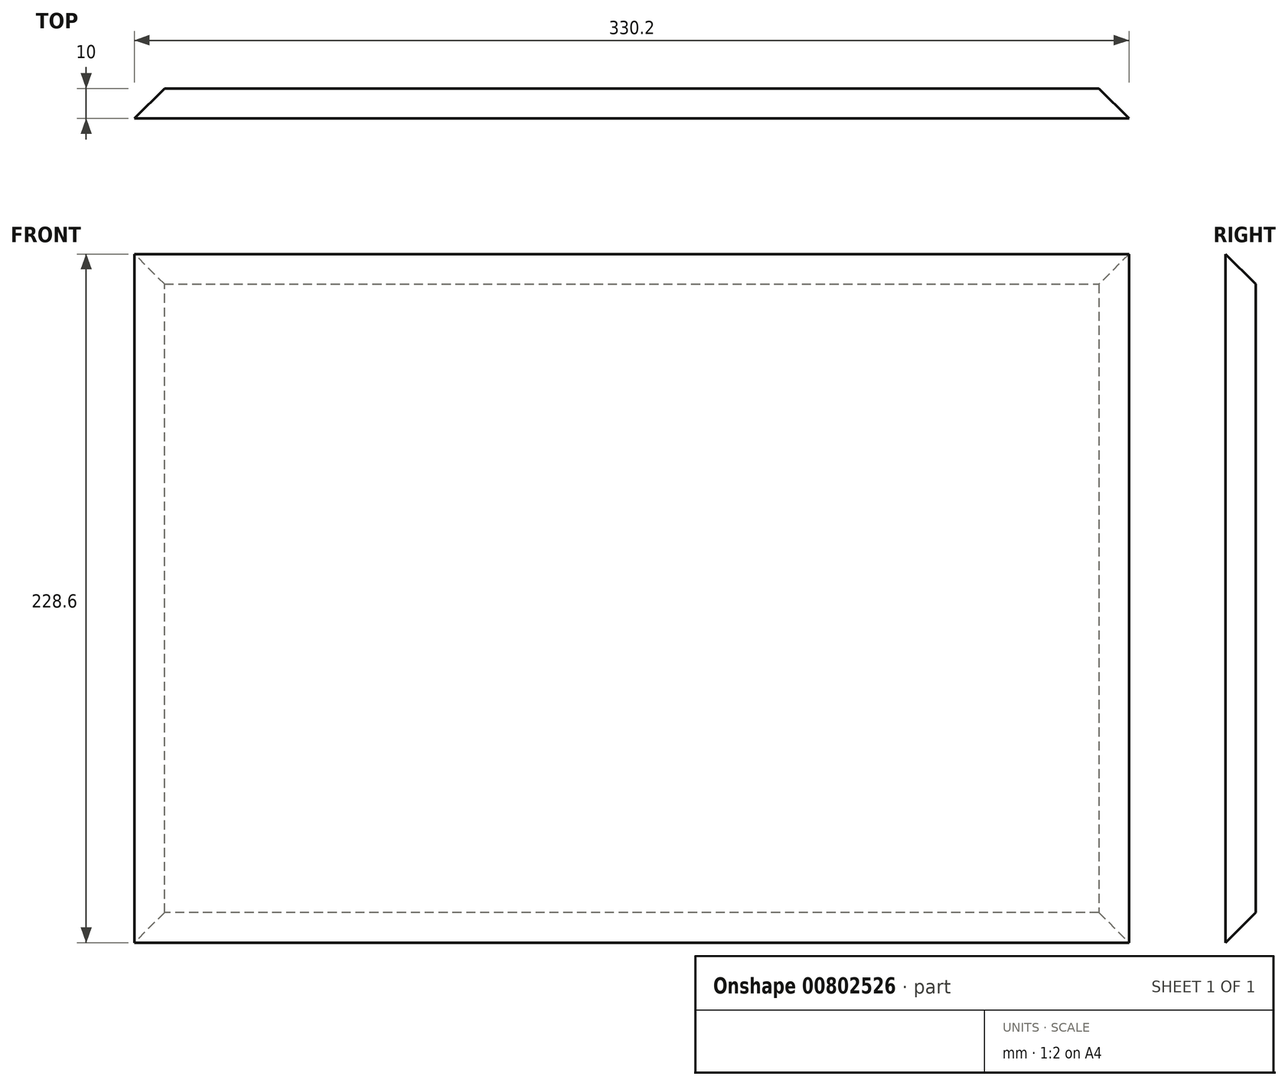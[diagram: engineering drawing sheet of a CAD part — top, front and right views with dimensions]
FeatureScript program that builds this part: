
annotation { "Feature Type Name" : "Feature", "Feature Type Description" : "" }
export const myFeature = defineFeature(function(context is Context, id is Id, definition is map)
    precondition{}
    {
        {
            var Q0;
            Q0=qCreatedBy(makeId("Front.planeOp"),FACE);
            var sketch = newSketch(context, id + "F0", { "sketchPlane" : qUnion([Q0])});
            skLineSegment(sketch, "E0.bottom", {"start": v(165.1, 114.3) * mm, "end": v(-165.1, 114.3) * mm});
            skLineSegment(sketch, "E0.top", {"start": v(165.1, -114.3) * mm, "end": v(-165.1, -114.3) * mm});
            skLineSegment(sketch, "E0.left", {"start": v(165.1, 114.3) * mm, "end": v(165.1, -114.3) * mm});
            skLineSegment(sketch, "E0.right", {"start": v(-165.1, 114.3) * mm, "end": v(-165.1, -114.3) * mm});
            skPoint(sketch, "E0.middle", {"position": v(0, 0) * mm});
            skSolve(sketch);
        }
        {
            var Q0;
            Q0=makeQuery(id+"F0.imprint","IMPRINT",FACE,{"disambiguationData":[TD([[makeQuery(id+"F0.imprint","IMPRINT",EDGE,{"derivedFrom":sQuery(id+"F0.wireOp",EDGE,"E0.bottom")}),1.0]])]});
            var sketch = newSketch(context, id + "F1", { "sketchPlane" : qUnion([Q0])});
            skLineSegment(sketch, "E1", {"start": v(-112.44, 43.6) * mm, "end": v(115.5, 43.6) * mm, "construction": true});
            skLineSegment(sketch, "E2.MirrorCS", {"start": v(-112.44, -43.6) * mm, "end": v(115.5, -43.6) * mm, "construction": true});
            skSolve(sketch);
        }
        {
            var Q0;
            Q0=makeQuery(id+"F1.imprint","IMPRINT",FACE,{"disambiguationData":[TD([[makeQuery(id+"F1.imprint","IMPRINT",EDGE,{"derivedFrom":makeQuery(id+"F0.imprint","IMPRINT",EDGE,{"derivedFrom":sQuery(id+"F0.wireOp",EDGE,"E0.bottom")})}),1.0]])]});
            extrude(context, id + "F2", {"entities" : qUnion([Q0]), "depth" : 10 * mm, "offsetDistance" : 25.4 * mm});
        }
        {
            var Q0;
            Q0=makeQuery(id+"F2.opExtrude","CAP_EDGE",EDGE,{"disambiguationData":[OSD([sQuery(id+"F0.wireOp",EDGE,"E0.bottom")])],"isStart":true});
            var Q1;
            Q1=makeQuery(id+"F2.opExtrude","CAP_EDGE",EDGE,{"disambiguationData":[OSD([sQuery(id+"F0.wireOp",EDGE,"E0.left")])],"isStart":true});
            var Q2;
            Q2=makeQuery(id+"F2.opExtrude","CAP_EDGE",EDGE,{"disambiguationData":[OSD([sQuery(id+"F0.wireOp",EDGE,"E0.right")])],"isStart":true});
            var Q3;
            Q3=makeQuery(id+"F2.opExtrude","CAP_EDGE",EDGE,{"disambiguationData":[OSD([sQuery(id+"F0.wireOp",EDGE,"E0.top")])],"isStart":true});
            chamfer(context, id + "F3", {"entities" : qUnion([Q0, Q1, Q2, Q3]), "width" : 10 * mm, "tangentPropagation" : true});
        }
    });
